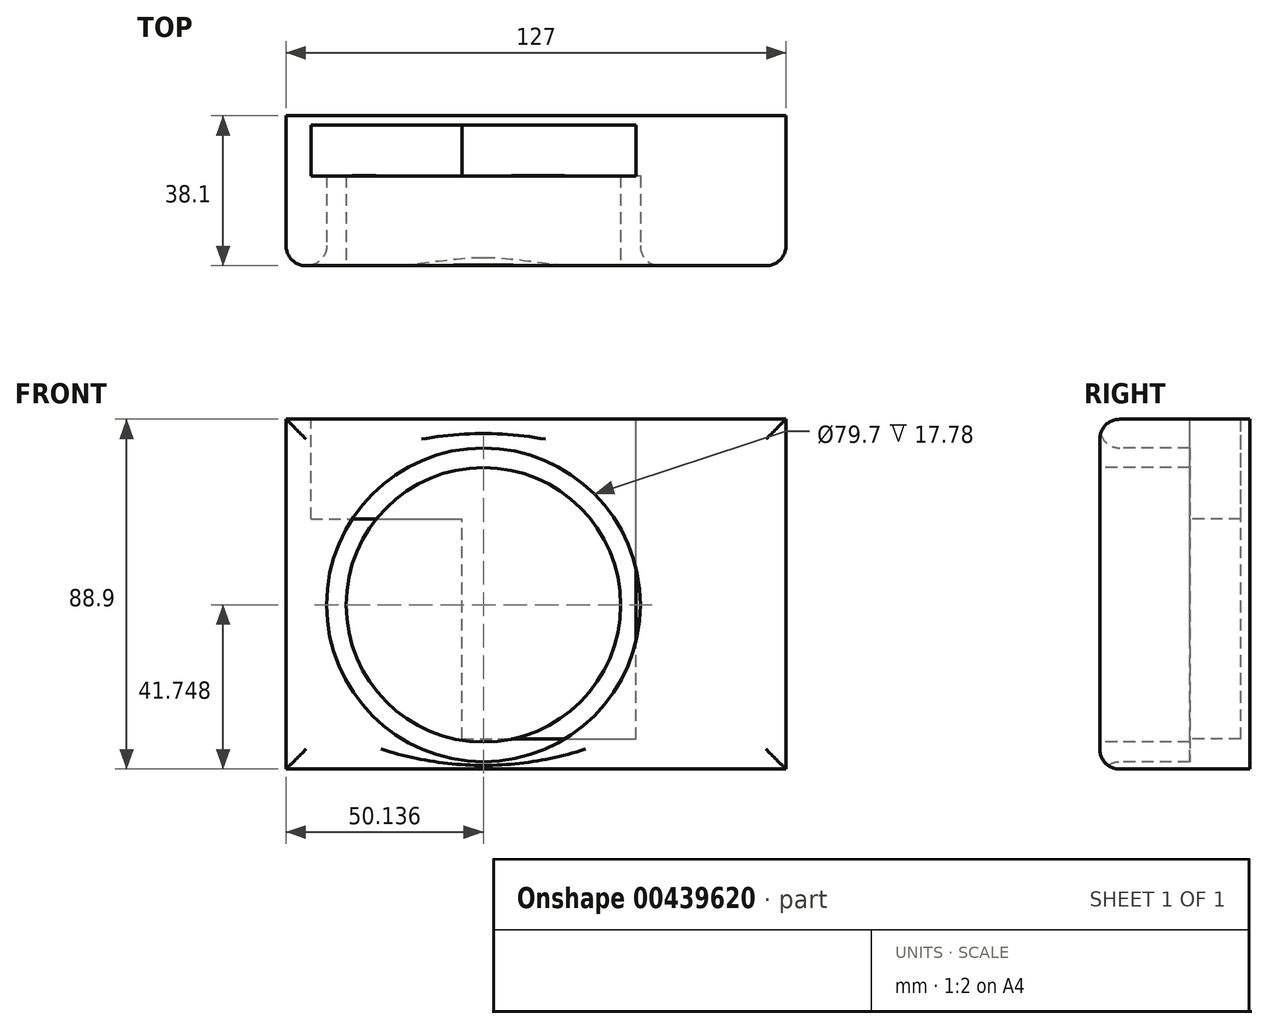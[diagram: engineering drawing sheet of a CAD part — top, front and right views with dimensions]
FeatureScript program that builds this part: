
annotation { "Feature Type Name" : "Feature", "Feature Type Description" : "" }
export const myFeature = defineFeature(function(context is Context, id is Id, definition is map)
    precondition{}
    {
        {
            var Q0;
            Q0=qCreatedBy(makeId("Front.planeOp"),FACE);
            var sketch = newSketch(context, id + "F0", { "sketchPlane" : qUnion([Q0])});
            skLineSegment(sketch, "E0.bottom", {"start": v(-127, 13.37) * mm, "end": v(0, 13.37) * mm});
            skLineSegment(sketch, "E0.top", {"start": v(-127, -75.53) * mm, "end": v(0, -75.53) * mm});
            skLineSegment(sketch, "E0.left", {"start": v(-127, 13.37) * mm, "end": v(-127, -75.53) * mm});
            skLineSegment(sketch, "E0.right", {"start": v(0, 13.37) * mm, "end": v(0, -75.53) * mm});
            skSolve(sketch);
        }
        {
            var Q0;
            Q0 = qSketchRegion(id + "F0", true);
            extrude(context, id + "F1", {"entities" : qUnion([Q0]), "depth" : 38.1 * mm});
        }
        {
            var Q0;
            Q0=makeQuery(id+"F1.opExtrude","SWEPT_FACE",FACE,{"disambiguationData":[OSD([sQuery(id+"F0.wireOp",EDGE,"E0.bottom")])]});
            var sketch = newSketch(context, id + "F2", { "sketchPlane" : qUnion([Q0])});
            skLineSegment(sketch, "E1.bottom", {"start": v(-120.7, -2.31) * mm, "end": v(-38.16, -2.31) * mm});
            skLineSegment(sketch, "E1.top", {"start": v(-120.7, -15.27) * mm, "end": v(-38.16, -15.27) * mm});
            skLineSegment(sketch, "E1.left", {"start": v(-120.7, -2.31) * mm, "end": v(-120.7, -15.27) * mm});
            skLineSegment(sketch, "E1.right", {"start": v(-38.16, -2.31) * mm, "end": v(-38.16, -15.27) * mm});
            skSolve(sketch);
        }
        {
            var Q0;
            Q0=makeQuery(id+"F2.imprint","IMPRINT",FACE,{"disambiguationData":[TD([[makeQuery(id+"F2.imprint","IMPRINT",EDGE,{"derivedFrom":sQuery(id+"F2.wireOp",EDGE,"E1.bottom")}),1.0]])]});
            extrude(context, id + "F3", {"entities" : qUnion([Q0]), "operationType" : NewBodyOperationType.ADD, "oppositeDirection" : true, "depth" : 25.4 * mm});
        }
        {
            var Q0;
            Q0=makeQuery(id+"F2.imprint","IMPRINT",FACE,{"disambiguationData":[TD([[makeQuery(id+"F2.imprint","IMPRINT",EDGE,{"derivedFrom":sQuery(id+"F2.wireOp",EDGE,"E1.bottom")}),-1.0]])]});
            extrude(context, id + "F4", {"entities" : qUnion([Q0]), "operationType" : NewBodyOperationType.REMOVE, "oppositeDirection" : true, "depth" : 25.4 * mm});
        }
        {
            var Q0;
            Q0=makeQuery(id+"F1.opExtrude","SWEPT_FACE",FACE,{"disambiguationData":[OSD([sQuery(id+"F0.wireOp",EDGE,"E0.bottom")])]});
            var sketch = newSketch(context, id + "F5", { "sketchPlane" : qUnion([Q0])});
            skLineSegment(sketch, "E2.bottom", {"start": v(-82.34, -2.31) * mm, "end": v(-38.16, -2.31) * mm});
            skLineSegment(sketch, "E2.top", {"start": v(-82.34, -15.27) * mm, "end": v(-38.16, -15.27) * mm});
            skLineSegment(sketch, "E2.left", {"start": v(-82.34, -2.31) * mm, "end": v(-82.34, -15.27) * mm});
            skLineSegment(sketch, "E2.right", {"start": v(-38.16, -2.31) * mm, "end": v(-38.16, -15.27) * mm});
            skSolve(sketch);
        }
        {
            var Q0;
            Q0=makeQuery(id+"F5.imprint","IMPRINT",FACE,{"disambiguationData":[TD([[makeQuery(id+"F5.imprint","IMPRINT",EDGE,{"derivedFrom":sQuery(id+"F5.wireOp",EDGE,"E2.bottom")}),-1.0]])]});
            extrude(context, id + "F6", {"entities" : qUnion([Q0]), "operationType" : NewBodyOperationType.REMOVE, "oppositeDirection" : true, "depth" : 81.28 * mm});
        }
        {
            var Q0;
            Q0=makeQuery(id+"F1.opExtrude","CAP_FACE",FACE,{"disambiguationData":[OSD([sQuery(id+"F0.wireOp",EDGE,"E0.bottom"),sQuery(id+"F0.wireOp",EDGE,"E0.top"),sQuery(id+"F0.wireOp",EDGE,"E0.left"),sQuery(id+"F0.wireOp",EDGE,"E0.right")])],"isStart":false});
            var sketch = newSketch(context, id + "F7", { "sketchPlane" : qUnion([Q0])});
            skCircle(sketch, "E3", {"center": v(-76.86, -33.78) * mm, "radius": 39.85 * mm});
            skCircle(sketch, "E4", {"center": v(-76.86, -33.78) * mm, "radius": 34.88 * mm});
            skCircle(sketch, "E5", {"center": v(-76.86, -33.78) * mm, "radius": 30.48 * mm});
            skCircle(sketch, "E6", {"center": v(-76.86, -33.78) * mm, "radius": 26.55 * mm});
            skCircle(sketch, "E7", {"center": v(-76.86, -33.78) * mm, "radius": 22.43 * mm});
            skCircle(sketch, "E8", {"center": v(-76.86, -33.78) * mm, "radius": 19.3 * mm});
            skCircle(sketch, "E9", {"center": v(-76.86, -33.78) * mm, "radius": 16 * mm});
            skCircle(sketch, "E10", {"center": v(-76.86, -33.78) * mm, "radius": 13.26 * mm});
            skCircle(sketch, "E11", {"center": v(-76.86, -33.78) * mm, "radius": 10.54 * mm});
            skCircle(sketch, "E12", {"center": v(-76.86, -33.78) * mm, "radius": 8 * mm});
            skCircle(sketch, "E13", {"center": v(-76.86, -33.78) * mm, "radius": 5.34 * mm});
            skSolve(sketch);
        }
        {
            var Q0;
            Q0=makeQuery(id+"F7.imprint","IMPRINT",FACE,{"disambiguationData":[TD([[makeQuery(id+"F7.imprint","IMPRINT",EDGE,{"derivedFrom":sQuery(id+"F7.wireOp",EDGE,"E3")}),1.0]])]});
            extrude(context, id + "F8", {"entities" : qUnion([Q0]), "operationType" : NewBodyOperationType.REMOVE, "oppositeDirection" : true, "depth" : 22.86 * mm});
        }
        {
            var Q0;
            {var subQ0=sQuery(id+"F0.wireOp",EDGE,"E0.left");var subQ1=sQuery(id+"F0.wireOp",EDGE,"E0.top");var subQ2=sQuery(id+"F0.wireOp",EDGE,"E0.right");var subQ3=sQuery(id+"F0.wireOp",EDGE,"E0.bottom");Q0=makeQuery(id+"F8.boolean.opBoolean","SPLIT",FACE,{"disambiguationData":[TD([makeQuery(id+"F1.opExtrude","SWEPT_FACE",FACE,{"disambiguationData":[OSD([subQ3])]})])],"derivedFrom":makeQuery(id+"F1.opExtrude","CAP_FACE",FACE,{"disambiguationData":[OSD([subQ3,subQ1,subQ0,subQ2])],"isStart":false})});}
            fillet(context, id + "F9", {"entities" : qUnion([Q0]), "radius" : 5.08 * mm, "tangentPropagation" : true, "allowEdgeOverflow" : false});
        }
    });
